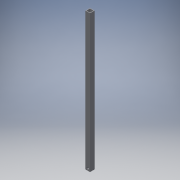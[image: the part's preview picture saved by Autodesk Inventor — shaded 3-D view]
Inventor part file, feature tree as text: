
AUTODESK INVENTOR PART (.ipt)
format: ipt  version: 2016 (Build 200138000, 138)  size: 111,104 bytes
history: native  units: in
note: dims shown in document units (in); Inventor stores cm internally (conversion verified against a paired STEP export)
features: extrude x2, sketch x2
ambient origin geometry x8: Origin, YZ Plane, XZ Plane, XY Plane, X Axis, Y Axis, Z Axis, Center Point
bodies: Solid1 (feature_tree)
feature tree (4):
  extrude  "Extrusion1"  Depth=1.0in
  extrude  "Extrusion2"  Depth=30.0in TaperAngle=0.0deg
  sketch  "Sketch1"  dims[d0=1.0in d1=1.0in]
  sketch  "Sketch2"  dims[d2=0.125in d3=30.0in d4=0.0in d5=0.5in d6=0.5in d7=0.5in d8=1.0in d9=0.0in d10=0.5in d11=0.5in d12=0.5in]
